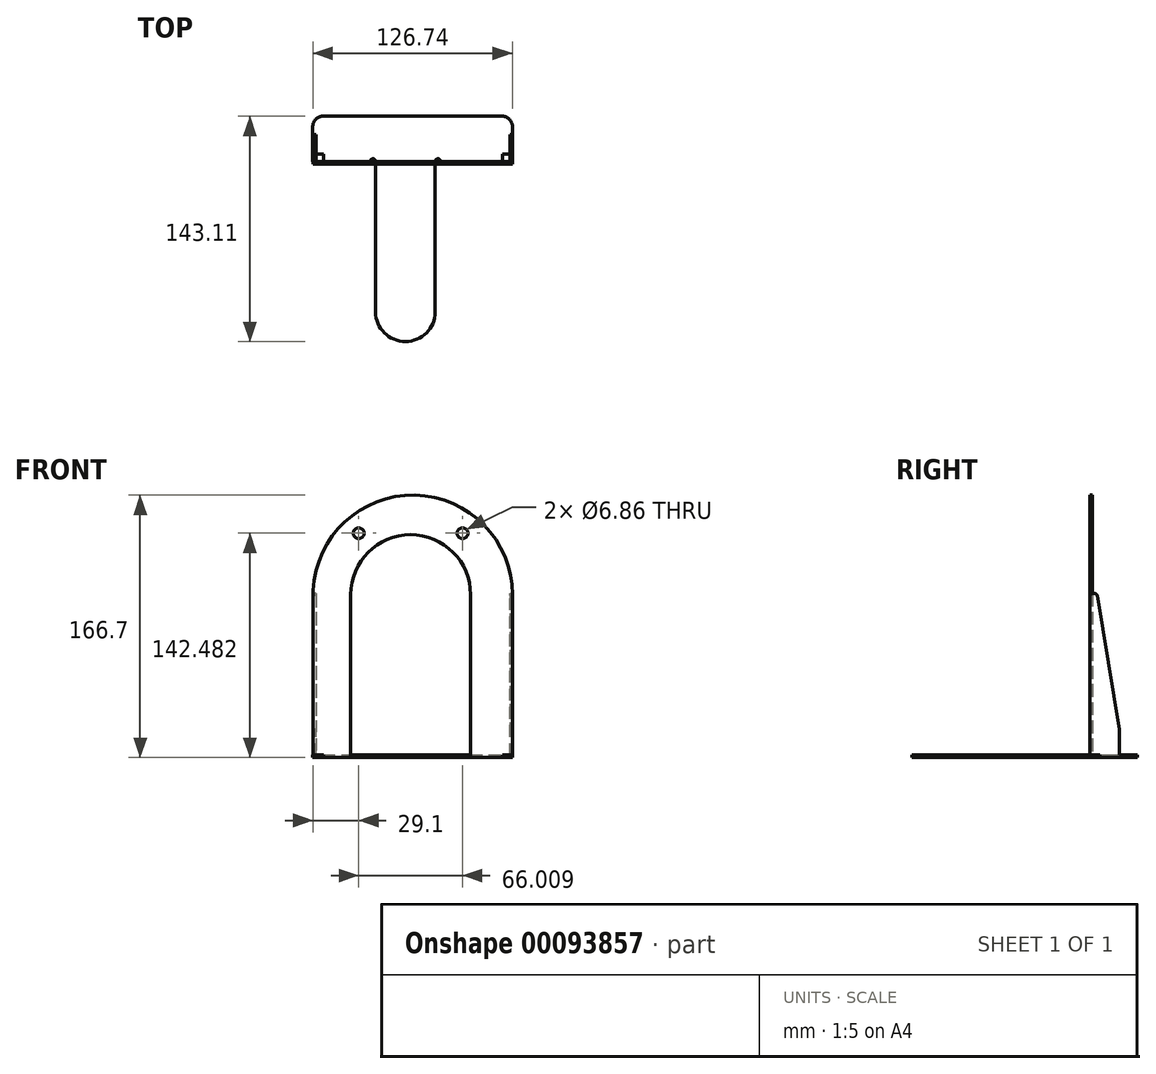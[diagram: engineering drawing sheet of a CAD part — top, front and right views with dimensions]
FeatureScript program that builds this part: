
annotation { "Feature Type Name" : "Feature", "Feature Type Description" : "" }
export const myFeature = defineFeature(function(context is Context, id is Id, definition is map)
    precondition{}
    {
        {
            var Q0;
            Q0=qCreatedBy(makeId("Top.planeOp"),FACE);
            var sketch = newSketch(context, id + "F0", { "sketchPlane" : qUnion([Q0])});
            skLineSegment(sketch, "E0", {"start": v(0, 0) * mm, "end": v(0, -95.5) * mm});
            skLineSegment(sketch, "E1", {"start": v(37.85, 0) * mm, "end": v(37.85, -95.5) * mm});
            skPoint(sketch, "E2", {"position": v(18.92, -95.5) * mm});
            skArc(sketch, "E3", {"start": v(0, -95.5) * mm, "mid": v(18.92, -114.43) * mm, "end": v(37.85, -95.5) * mm});
            skLineSegment(sketch, "E4", {"start": v(-39.88, 0) * mm, "end": v(-3.43, 0) * mm});
            skLineSegment(sketch, "E5", {"start": v(-33.53, 28.68) * mm, "end": v(80.51, 28.68) * mm});
            skLineSegment(sketch, "E6", {"start": v(-39.88, 0) * mm, "end": v(-39.88, 22.33) * mm});
            skLineSegment(sketch, "E7", {"start": v(86.86, 22.33) * mm, "end": v(86.86, 0) * mm});
            skPoint(sketch, "E8.visualSharp", {"position": v(-39.88, 28.68) * mm});
            skArc(sketch, "E8.filletArc", {"start": v(-33.53, 28.68) * mm, "mid": v(-38.02, 26.82) * mm, "end": v(-39.88, 22.33) * mm});
            skPoint(sketch, "E9.visualSharp", {"position": v(86.86, 28.68) * mm});
            skArc(sketch, "E9.filletArc", {"start": v(86.86, 22.33) * mm, "mid": v(85, 26.82) * mm, "end": v(80.51, 28.68) * mm});
            skArc(sketch, "E10", {"start": v(41.28, 0) * mm, "mid": v(39.56, 1.71) * mm, "end": v(37.85, 0) * mm});
            skArc(sketch, "E11", {"start": v(0, 0) * mm, "mid": v(-1.71, 1.71) * mm, "end": v(-3.43, 0) * mm});
            skLineSegment(sketch, "E12.trimOffspring", {"start": v(41.28, 0) * mm, "end": v(86.86, 0) * mm});
            skSolve(sketch);
        }
        {
            var Q0;
            Q0 = qSketchRegion(id + "F0", true);
            extrude(context, id + "F1", {"entities" : qUnion([Q0]), "depth" : 1.6 * mm});
        }
        {
            var Q0;
            Q0=makeQuery(id+"F1.opExtrude","SWEPT_FACE",FACE,{"disambiguationData":[OSD([sQuery(id+"F0.wireOp",EDGE,"E12.trimOffspring")])]});
            var sketch = newSketch(context, id + "F2", { "sketchPlane" : qUnion([Q0])});
            skLineSegment(sketch, "E13", {"start": v(86.86, 0) * mm, "end": v(86.86, 103.45) * mm});
            skLineSegment(sketch, "E14", {"start": v(86.86, 103.45) * mm, "end": v(60.32, 103.45) * mm, "construction": true});
            skArc(sketch, "E15", {"start": v(86.86, 103.45) * mm, "mid": v(25, 166.68) * mm, "end": v(-39.57, 106.24) * mm});
            skLineSegment(sketch, "E16", {"start": v(-39.57, 106.24) * mm, "end": v(-39.57, 0) * mm});
            skArc(sketch, "E17", {"start": v(60.32, 103.45) * mm, "mid": v(22.22, 141.55) * mm, "end": v(-15.88, 103.45) * mm});
            skLineSegment(sketch, "E18", {"start": v(-39.57, 0) * mm, "end": v(-15.88, 0) * mm});
            skLineSegment(sketch, "E19", {"start": v(60.32, 103.45) * mm, "end": v(60.32, 0) * mm});
            skLineSegment(sketch, "E20", {"start": v(-15.88, 103.45) * mm, "end": v(-15.88, 0) * mm});
            skPoint(sketch, "E20.endSnap0", {"position": v(64.07, 0) * mm});
            skLineSegment(sketch, "E21.trimOffspring", {"start": v(60.32, 0) * mm, "end": v(86.86, 0) * mm});
            skLineSegment(sketch, "E22", {"start": v(22.22, 103.45) * mm, "end": v(22.22, 155.39) * mm, "construction": true});
            skCircle(sketch, "E23", {"center": v(55.23, 142.48) * mm, "radius": 3.43 * mm});
            skCircle(sketch, "E24.MirrorC", {"center": v(-10.78, 142.48) * mm, "radius": 3.43 * mm});
            skPoint(sketch, "E25.orphan", {"position": v(45.87, 133.33) * mm});
            skPoint(sketch, "E26.orphan", {"position": v(64.6, 151.63) * mm});
            skSolve(sketch);
        }
        {
            var Q0;
            Q0 = qSketchRegion(id + "F2", true);
            extrude(context, id + "F3", {"entities" : qUnion([Q0]), "operationType" : NewBodyOperationType.ADD, "depth" : 1.6 * mm});
        }
        {
            var Q0;
            Q0=makeQuery(id+"F3.boolean.opBoolean","MERGE",FACE,{"derivedFrom":[makeQuery(id+"F1.opExtrude","SWEPT_FACE",FACE,{"disambiguationData":[OSD([sQuery(id+"F0.wireOp",EDGE,"E7")])]}),makeQuery(id+"F3.opExtrude","SWEPT_FACE",FACE,{"disambiguationData":[OSD([sQuery(id+"F2.wireOp",EDGE,"E13")])]})]});
            var sketch = newSketch(context, id + "F4", { "sketchPlane" : qUnion([Q0])});
            skLineSegment(sketch, "E27", {"start": v(-1.6, 0) * mm, "end": v(-1.6, 101.75) * mm});
            skArc(sketch, "E28", {"start": v(3.2, 102.91) * mm, "mid": v(0.34, 104.22) * mm, "end": v(-1.6, 101.75) * mm});
            skLineSegment(sketch, "E29", {"start": v(-1.6, 0) * mm, "end": v(17.2, 0) * mm});
            skLineSegment(sketch, "E30", {"start": v(17.2, 0) * mm, "end": v(17.2, 17.78) * mm});
            skLineSegment(sketch, "E31", {"start": v(3.2, 102.91) * mm, "end": v(17.2, 17.78) * mm});
            skSolve(sketch);
        }
        {
            var Q0;
            Q0 = qSketchRegion(id + "F4", true);
            extrude(context, id + "F5", {"entities" : qUnion([Q0]), "operationType" : NewBodyOperationType.ADD, "oppositeDirection" : true, "depth" : 1.6 * mm});
        }
        {
            var Q0;
            Q0=makeQuery(id+"F3.opExtrude","CAP_FACE",FACE,{"disambiguationData":[OSD([sQuery(id+"F2.wireOp",EDGE,"E13"),sQuery(id+"F2.wireOp",EDGE,"E15"),sQuery(id+"F2.wireOp",EDGE,"E16"),sQuery(id+"F2.wireOp",EDGE,"E17"),sQuery(id+"F2.wireOp",EDGE,"E18"),sQuery(id+"F2.wireOp",EDGE,"E19"),sQuery(id+"F2.wireOp",EDGE,"E20"),sQuery(id+"F2.wireOp",EDGE,"E21.trimOffspring"),sQuery(id+"F2.wireOp",EDGE,"E23"),sQuery(id+"F2.wireOp",EDGE,"E24.MirrorC")])],"isStart":false});
            var sketch = newSketch(context, id + "F6", { "sketchPlane" : qUnion([Q0])});
            skPoint(sketch, "E32.0", {"position": v(86.86, 0) * mm});
            skSolve(sketch);
        }
        {
            var Q0;
            Q0=makeQuery(id+"F3.opExtrude","SWEPT_FACE",FACE,{"disambiguationData":[OSD([sQuery(id+"F2.wireOp",EDGE,"E16")])]});
            var sketch = newSketch(context, id + "F7", { "sketchPlane" : qUnion([Q0])});
            skArc(sketch, "E33.0", {"start": v(-3.2, 102.91) * mm, "mid": v(-0.34, 104.22) * mm, "end": v(1.6, 101.75) * mm});
            skLineSegment(sketch, "E34.0", {"start": v(-3.2, 102.91) * mm, "end": v(-17.2, 17.78) * mm});
            skLineSegment(sketch, "E35.0", {"start": v(-17.2, 0) * mm, "end": v(-17.2, 17.78) * mm});
            skLineSegment(sketch, "E36.0", {"start": v(1.6, 0) * mm, "end": v(-17.2, 0) * mm});
            skLineSegment(sketch, "E37.0", {"start": v(1.6, 0) * mm, "end": v(1.6, 101.75) * mm});
            skSolve(sketch);
        }
        {
            var Q0;
            Q0 = qSketchRegion(id + "F7", true);
            extrude(context, id + "F8", {"entities" : qUnion([Q0]), "operationType" : NewBodyOperationType.ADD, "oppositeDirection" : true, "depth" : 1.6 * mm});
        }
        {
            var Q0;
            Q0=makeQuery(id+"F1.opExtrude","CAP_FACE",FACE,{"disambiguationData":[OSD([sQuery(id+"F0.wireOp",EDGE,"E0"),sQuery(id+"F0.wireOp",EDGE,"E1"),sQuery(id+"F0.wireOp",EDGE,"E3"),sQuery(id+"F0.wireOp",EDGE,"E4"),sQuery(id+"F0.wireOp",EDGE,"E5"),sQuery(id+"F0.wireOp",EDGE,"E6"),sQuery(id+"F0.wireOp",EDGE,"E7"),sQuery(id+"F0.wireOp",EDGE,"E8.filletArc"),sQuery(id+"F0.wireOp",EDGE,"E9.filletArc"),sQuery(id+"F0.wireOp",EDGE,"E10"),sQuery(id+"F0.wireOp",EDGE,"E11"),sQuery(id+"F0.wireOp",EDGE,"E12.trimOffspring")])],"isStart":false});
            var sketch = newSketch(context, id + "F9", { "sketchPlane" : qUnion([Q0])});
            skPoint(sketch, "E38.0", {"position": v(86.86, -1.6) * mm});
            skLineSegment(sketch, "E39", {"start": v(86.86, -1.6) * mm, "end": v(86.86, 4.75) * mm});
            skLineSegment(sketch, "E40", {"start": v(86.86, 4.75) * mm, "end": v(80.51, 4.75) * mm});
            skLineSegment(sketch, "E41", {"start": v(80.51, 4.75) * mm, "end": v(80.51, -1.6) * mm});
            skLineSegment(sketch, "E42", {"start": v(86.86, -1.6) * mm, "end": v(80.51, -1.6) * mm});
            skPoint(sketch, "E43.0", {"position": v(-39.57, -1.6) * mm});
            skLineSegment(sketch, "E44", {"start": v(-39.57, -1.6) * mm, "end": v(-33.22, -1.6) * mm});
            skLineSegment(sketch, "E45", {"start": v(-33.22, -1.6) * mm, "end": v(-33.22, 4.75) * mm});
            skLineSegment(sketch, "E46", {"start": v(-33.22, 4.75) * mm, "end": v(-39.57, 4.75) * mm});
            skLineSegment(sketch, "E47", {"start": v(-39.57, -1.6) * mm, "end": v(-39.57, 4.75) * mm});
            skSolve(sketch);
        }
        {
            var Q0;
            Q0=makeQuery(id+"F3.boolean.opBoolean","MERGE",FACE,{"derivedFrom":[makeQuery(id+"F1.opExtrude","CAP_FACE",FACE,{"disambiguationData":[OSD([sQuery(id+"F0.wireOp",EDGE,"E0"),sQuery(id+"F0.wireOp",EDGE,"E1"),sQuery(id+"F0.wireOp",EDGE,"E3"),sQuery(id+"F0.wireOp",EDGE,"E4"),sQuery(id+"F0.wireOp",EDGE,"E5"),sQuery(id+"F0.wireOp",EDGE,"E6"),sQuery(id+"F0.wireOp",EDGE,"E7"),sQuery(id+"F0.wireOp",EDGE,"E8.filletArc"),sQuery(id+"F0.wireOp",EDGE,"E9.filletArc"),sQuery(id+"F0.wireOp",EDGE,"E10"),sQuery(id+"F0.wireOp",EDGE,"E11"),sQuery(id+"F0.wireOp",EDGE,"E12.trimOffspring")])],"isStart":true}),makeQuery(id+"F3.opExtrude","SWEPT_FACE",FACE,{"disambiguationData":[OSD([sQuery(id+"F2.wireOp",EDGE,"E18")])]}),makeQuery(id+"F3.opExtrude","SWEPT_FACE",FACE,{"disambiguationData":[OSD([sQuery(id+"F2.wireOp",EDGE,"E21.trimOffspring")])]})]});
            var sketch = newSketch(context, id + "F10", { "sketchPlane" : qUnion([Q0])});
            skLineSegment(sketch, "E48.0", {"start": v(86.86, -4.75) * mm, "end": v(80.51, -4.75) * mm});
            skLineSegment(sketch, "E49.0", {"start": v(80.51, -4.75) * mm, "end": v(80.51, 1.6) * mm});
            skLineSegment(sketch, "E50.0", {"start": v(86.86, 1.6) * mm, "end": v(80.51, 1.6) * mm});
            skLineSegment(sketch, "E51.0", {"start": v(86.86, 1.6) * mm, "end": v(86.86, -4.75) * mm});
            skLineSegment(sketch, "E52.0", {"start": v(-39.57, 1.6) * mm, "end": v(-33.22, 1.6) * mm});
            skLineSegment(sketch, "E53.0", {"start": v(-33.22, -4.75) * mm, "end": v(-39.57, -4.75) * mm});
            skLineSegment(sketch, "E54.0", {"start": v(-33.22, 1.6) * mm, "end": v(-33.22, -4.75) * mm});
            skLineSegment(sketch, "E55.0", {"start": v(-39.57, 1.6) * mm, "end": v(-39.57, -4.75) * mm});
            skSolve(sketch);
        }
        {
            var Q0;
            Q0 = qSketchRegion(id + "F10", true);
            extrude(context, id + "F11", {"entities" : qUnion([Q0]), "operationType" : NewBodyOperationType.REMOVE, "oppositeDirection" : true, "depth" : 1.63 * mm});
        }
    });
